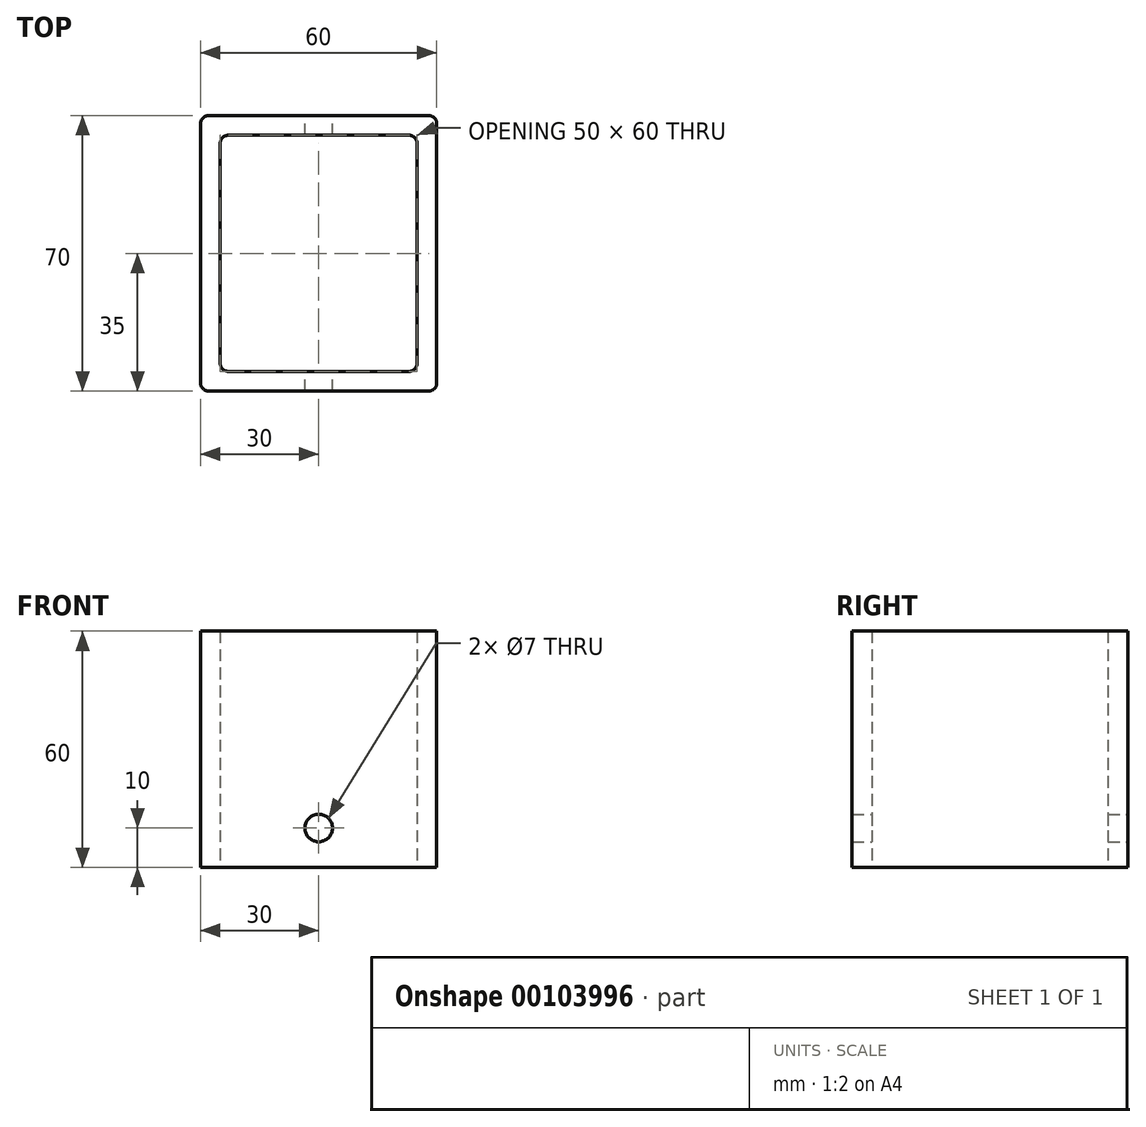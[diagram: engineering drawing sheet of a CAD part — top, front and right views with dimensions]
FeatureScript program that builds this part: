
annotation { "Feature Type Name" : "Feature", "Feature Type Description" : "" }
export const myFeature = defineFeature(function(context is Context, id is Id, definition is map)
    precondition{}
    {
        {
            var Q0;
            Q0=qCreatedBy(makeId("Top.planeOp"),FACE);
            var sketch = newSketch(context, id + "F0", { "sketchPlane" : qUnion([Q0])});
            skLineSegment(sketch, "E0.bottom", {"start": v(-30, 35) * mm, "end": v(30, 35) * mm});
            skLineSegment(sketch, "E0.top", {"start": v(-30, -35) * mm, "end": v(30, -35) * mm});
            skLineSegment(sketch, "E0.left", {"start": v(-30, 35) * mm, "end": v(-30, -35) * mm});
            skLineSegment(sketch, "E0.right", {"start": v(30, 35) * mm, "end": v(30, -35) * mm});
            skPoint(sketch, "E0.middle", {"position": v(0, 0) * mm});
            skLineSegment(sketch, "E1.bottom", {"start": v(-25, 30) * mm, "end": v(25, 30) * mm});
            skLineSegment(sketch, "E1.top", {"start": v(-25, -30) * mm, "end": v(25, -30) * mm});
            skLineSegment(sketch, "E1.left", {"start": v(-25, 30) * mm, "end": v(-25, -30) * mm});
            skLineSegment(sketch, "E1.right", {"start": v(25, 30) * mm, "end": v(25, -30) * mm});
            skSolve(sketch);
        }
        {
            var Q0;
            Q0=makeQuery(id+"F0.imprint","IMPRINT",FACE,{"disambiguationData":[TD([[makeQuery(id+"F0.imprint","IMPRINT",EDGE,{"derivedFrom":sQuery(id+"F0.wireOp",EDGE,"E0.bottom")}),-1.0]])]});
            extrude(context, id + "F1", {"entities" : qUnion([Q0]), "depth" : 60 * mm});
        }
        {
            var Q0;
            Q0=makeQuery(id+"F1.opExtrude","SWEPT_EDGE",EDGE,{"disambiguationData":[OSD([sQuery(id+"F0.wireOp",EDGE,"E0.bottom"),sQuery(id+"F0.wireOp",EDGE,"E0.right")])]});
            var Q1;
            Q1=makeQuery(id+"F1.opExtrude","SWEPT_EDGE",EDGE,{"disambiguationData":[OSD([sQuery(id+"F0.wireOp",EDGE,"E0.bottom"),sQuery(id+"F0.wireOp",EDGE,"E0.left")])]});
            var Q2;
            Q2=makeQuery(id+"F1.opExtrude","SWEPT_EDGE",EDGE,{"disambiguationData":[OSD([sQuery(id+"F0.wireOp",EDGE,"E0.top"),sQuery(id+"F0.wireOp",EDGE,"E0.right")])]});
            var Q3;
            Q3=makeQuery(id+"F1.opExtrude","SWEPT_EDGE",EDGE,{"disambiguationData":[OSD([sQuery(id+"F0.wireOp",EDGE,"E0.top"),sQuery(id+"F0.wireOp",EDGE,"E0.left")])]});
            var Q4;
            Q4=makeQuery(id+"F1.opExtrude","SWEPT_EDGE",EDGE,{"disambiguationData":[OSD([sQuery(id+"F0.wireOp",EDGE,"E1.bottom"),sQuery(id+"F0.wireOp",EDGE,"E1.left")])]});
            var Q5;
            Q5=makeQuery(id+"F1.opExtrude","SWEPT_EDGE",EDGE,{"disambiguationData":[OSD([sQuery(id+"F0.wireOp",EDGE,"E1.top"),sQuery(id+"F0.wireOp",EDGE,"E1.left")])]});
            var Q6;
            Q6=makeQuery(id+"F1.opExtrude","SWEPT_EDGE",EDGE,{"disambiguationData":[OSD([sQuery(id+"F0.wireOp",EDGE,"E1.top"),sQuery(id+"F0.wireOp",EDGE,"E1.right")])]});
            var Q7;
            Q7=makeQuery(id+"F1.opExtrude","SWEPT_EDGE",EDGE,{"disambiguationData":[OSD([sQuery(id+"F0.wireOp",EDGE,"E1.bottom"),sQuery(id+"F0.wireOp",EDGE,"E1.right")])]});
            fillet(context, id + "F2", {"entities" : qUnion([Q0, Q1, Q2, Q3, Q4, Q5, Q6, Q7]), "radius" : 2 * mm, "tangentPropagation" : true, "allowEdgeOverflow" : false});
        }
        {
            var Q0;
            Q0=makeQuery(id+"F1.opExtrude","SWEPT_FACE",FACE,{"disambiguationData":[OSD([sQuery(id+"F0.wireOp",EDGE,"E0.bottom")])]});
            var sketch = newSketch(context, id + "F3", { "sketchPlane" : qUnion([Q0])});
            skCircle(sketch, "E2", {"center": v(0, 10) * mm, "radius": 3.5 * mm});
            skSolve(sketch);
        }
        {
            var Q0;
            Q0=makeQuery(id+"F3.imprint","IMPRINT",FACE,{"disambiguationData":[TD([[makeQuery(id+"F3.imprint","IMPRINT",EDGE,{"derivedFrom":sQuery(id+"F3.wireOp",EDGE,"E2")}),1.0]])]});
            extrude(context, id + "F4", {"entities" : qUnion([Q0]), "operationType" : NewBodyOperationType.REMOVE, "oppositeDirection" : true, "depth" : 70 * mm});
        }
    });
